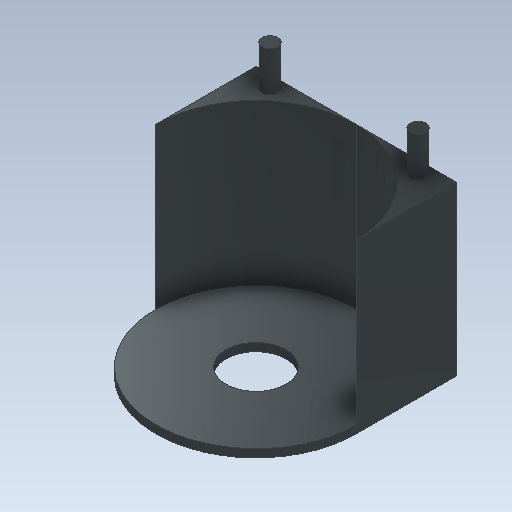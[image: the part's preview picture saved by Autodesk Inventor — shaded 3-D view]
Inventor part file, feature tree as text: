
AUTODESK INVENTOR PART (.ipt)
format: ipt  version: 2020.2 (Build 242310000, 310)  size: 158,208 bytes
history: native  units: in
note: dims shown in document units (in); Inventor stores cm internally (conversion verified against a paired STEP export)
features: extrude x6, sketch x6
ambient origin geometry x8: Origin, YZ Plane, XZ Plane, XY Plane, X Axis, Y Axis, Z Axis, Center Point
bodies: Solid1 (feature_tree)
feature tree (12):
  extrude  "Extrusion1"  Depth=1.9685in
  extrude  "Extrusion2"  Depth=0.3937in TaperAngle=0.0deg
  extrude  "Extrusion3"  Depth=0.1575in
  extrude  "Extrusion4"  Depth=1.6535in TaperAngle=0.0deg
  extrude  "Extrusion5"  Depth=0.3937in
  extrude  "Extrusion6"  Depth=0.3937in TaperAngle=0.0deg
  sketch  "Sketch1"  dims[d0=0.5906in d1=1.9685in]
  sketch  "Sketch2"  dims[d2=0.0787in d3=0.0in d4=0.3937in d5=0.0787in d6=0.0in d7=0.0in]
  sketch  "Sketch3"  dims[d8=0.1575in d9=0.1575in]
  sketch  "Sketch4"  dims[d10=1.5748in d11=0.0in d12=1.6535in d13=0.0in]
  sketch  "Sketch5"  dims[d14=0.3937in d15=0.0in d16=0.1575in]
  sketch  "Sketch6"  dims[d17=0.1575in d18=0.3937in d19=0.0in]
